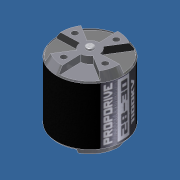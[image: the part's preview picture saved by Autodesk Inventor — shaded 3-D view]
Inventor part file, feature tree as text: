
AUTODESK INVENTOR PART (.ipt)
format: ipt  version: unknown  size: 358,912 bytes
history: native  units: mm
features: sketch x9, extrude x7, pattern_circular x4, chamfer x3, projected_geometry x3, other x2, hole x1, plane x1
ambient origin geometry x8: Origin, YZ Plane, XZ Plane, XY Plane, X Axis, Y Axis, Z Axis, Center Point
bodies: Solid1 (feature_tree)
feature tree (30):
  extrude  "Extrusion1"  Depth=30.0mm TaperAngle=0.0deg
  chamfer  "Chamfer1"  Distance=2.0mm Angle=45.0deg
  chamfer  "Chamfer2"  Distance=2.0mm Angle=45.0deg
  extrude  "Extrusion2"  Depth=1.4mm TaperAngle=0.0deg
  extrude  "Extrusion3"  Depth=16.0mm
  pattern_circular  "Circular Pattern1"  Count=3 Angle=360.0deg
  hole  "Hole1"  [1 undecoded]
  pattern_circular  "Circular Pattern2"  Count=4 Angle=360.0deg
  extrude  "Extrusion4"  Depth=1.0mm TaperAngle=0.0deg
  extrude  "Extrusion5"  Depth=0.2mm TaperAngle=45.0deg
  pattern_circular  "Circular Pattern3"  [2 undecoded]
  extrude  "Extrusion6"  Depth=9.0mm
  chamfer  "Chamfer3"  Distance=5.0mm
  extrude  "Extrusion7"  Depth=40.0mm TaperAngle=360.0deg
  pattern_circular  "Circular Pattern4"  [2 undecoded]
  plane  "Work Plane1"
  other  "Decal1"
  sketch  "Sketch1"  dims[d0=28.0mm d1=30.0mm d2=0.0mm d3=2.0mm d4=3.0mm d5=45.0deg d6=2.0mm d7=3.0mm d8=45.0deg]
  sketch  "Sketch2"  dims[d9=8.0mm d10=1.4mm d11=0.0mm]
  sketch  "Sketch3"  dims[d12=4.886922mm d13=16.0mm]
  sketch  "Sketch4"  dims[d14=2.4mm d15=0.0mm d16=30.0mm d17=360.0deg]
  sketch  "Sketch6"  dims[d19=8.0mm]
  projected_geometry  "Projected Loop1"
  projected_geometry  "Projected Loop2"
  sketch  "Sketch7"  dims[d20=2.013mm d21=4.0mm d22=4.0mm d23=2.0mm d24=90.0deg d25=4.0mm d26=20.594885mm d27=30.0mm d28=360.0deg]
  projected_geometry  "Projected Loop3"
  sketch  "Sketch8"  dims[d30=10.0mm d31=0.0mm]
  sketch  "Sketch9"  dims[d32=3.0mm d33=0.0mm d34=40.0mm d35=360.0deg]
  sketch  "Sketch10"  dims[d37=3.0mm d38=1.0mm d39=0.0mm d40=0.2mm d41=2.0mm d42=45.0deg d43=2.5mm d44=9.0mm d45=5.0mm d46=0.0mm d47=40.0mm d48=360.0deg]
  other  "Image2"
note: 5 required parameter values undecoded (feature->parameter linkage not recoverable at this tier; creation-order binding heuristic only, values carry confidence <= 0.55)
